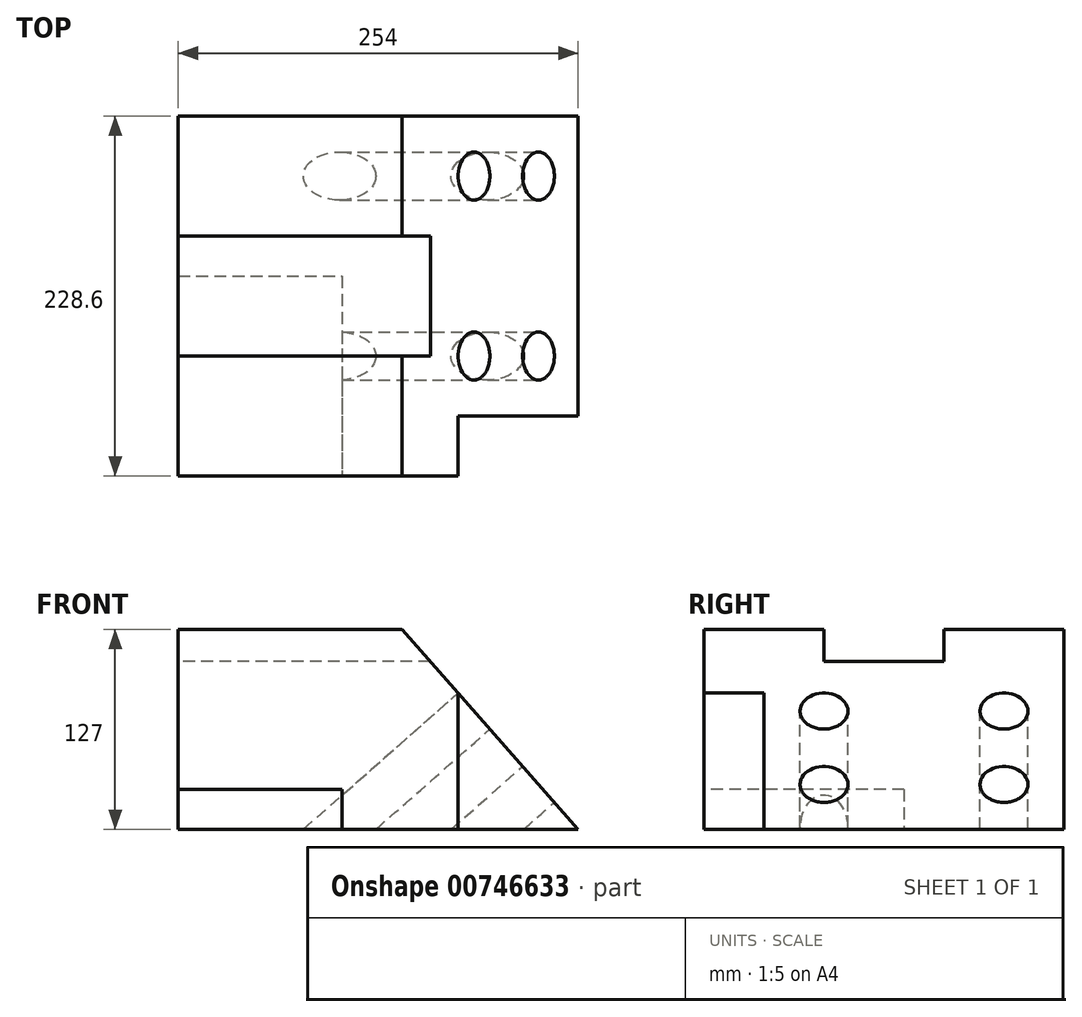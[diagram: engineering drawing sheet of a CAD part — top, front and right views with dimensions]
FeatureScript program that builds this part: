
annotation { "Feature Type Name" : "Feature", "Feature Type Description" : "" }
export const myFeature = defineFeature(function(context is Context, id is Id, definition is map)
    precondition{}
    {
        {
            var Q0;
            Q0=qCreatedBy(makeId("Front.planeOp"),FACE);
            var sketch = newSketch(context, id + "F0", { "sketchPlane" : qUnion([Q0])});
            skLineSegment(sketch, "E0.bottom", {"start": v(-127, 63.5) * mm, "end": v(127, 63.5) * mm});
            skLineSegment(sketch, "E0.top", {"start": v(-127, -63.5) * mm, "end": v(127, -63.5) * mm});
            skLineSegment(sketch, "E0.left", {"start": v(-127, 63.5) * mm, "end": v(-127, -63.5) * mm});
            skLineSegment(sketch, "E0.right", {"start": v(127, 63.5) * mm, "end": v(127, -63.5) * mm});
            skSolve(sketch);
        }
        {
            var Q0;
            Q0=makeQuery(id+"F0.imprint","IMPRINT",FACE,{"disambiguationData":[TD([[makeQuery(id+"F0.imprint","IMPRINT",EDGE,{"derivedFrom":sQuery(id+"F0.wireOp",EDGE,"E0.bottom")}),-1.0]])]});
            extrude(context, id + "F1", {"entities" : qUnion([Q0]), "oppositeDirection" : true, "depth" : 228.6 * mm, "offsetDistance" : 25.4 * mm});
        }
        {
            var Q0;
            Q0=makeQuery(id+"F1.opExtrude","CAP_FACE",FACE,{"disambiguationData":[OSD([sQuery(id+"F0.wireOp",EDGE,"E0.bottom"),sQuery(id+"F0.wireOp",EDGE,"E0.top"),sQuery(id+"F0.wireOp",EDGE,"E0.left"),sQuery(id+"F0.wireOp",EDGE,"E0.right")])],"isStart":true});
            var sketch = newSketch(context, id + "F2", { "sketchPlane" : qUnion([Q0])});
            skLineSegment(sketch, "E1", {"start": v(15.24, 63.5) * mm, "end": v(15.24, -63.5) * mm});
            skLineSegment(sketch, "E2", {"start": v(15.24, -63.5) * mm, "end": v(127, -63.5) * mm});
            skLineSegment(sketch, "E3", {"start": v(127, -63.5) * mm, "end": v(15.24, 63.5) * mm});
            skSolve(sketch);
        }
        {
            var Q0;
            {var subQ0=sQuery(id+"F2.wireOp",EDGE,"E3");Q0=makeQuery(id+"F2.imprint","IMPRINT",FACE,{"disambiguationData":[TD([[makeQuery(id+"F2.imprint","IMPRINT",EDGE,{"derivedFrom":subQ0}),-1.0]])]});}
            extrude(context, id + "F3", {"entities" : qUnion([Q0]), "operationType" : NewBodyOperationType.REMOVE, "oppositeDirection" : true, "depth" : 1270 * mm, "offsetDistance" : 25.4 * mm});
        }
        {
            var Q0;
            Q0=makeQuery(id+"F1.opExtrude","CAP_FACE",FACE,{"disambiguationData":[OSD([sQuery(id+"F0.wireOp",EDGE,"E0.bottom"),sQuery(id+"F0.wireOp",EDGE,"E0.top"),sQuery(id+"F0.wireOp",EDGE,"E0.left"),sQuery(id+"F0.wireOp",EDGE,"E0.right")])],"isStart":true});
            var sketch = newSketch(context, id + "F4", { "sketchPlane" : qUnion([Q0])});
            skLineSegment(sketch, "E4", {"start": v(127, -63.5) * mm, "end": v(50.8, 23.1) * mm});
            skLineSegment(sketch, "E5", {"start": v(50.8, 23.1) * mm, "end": v(50.8, -63.5) * mm});
            skLineSegment(sketch, "E6", {"start": v(50.8, -63.5) * mm, "end": v(127, -63.5) * mm});
            skSolve(sketch);
        }
        {
            var Q0;
            Q0=makeQuery(id+"F4.imprint","IMPRINT",FACE,{"disambiguationData":[TD([[makeQuery(id+"F4.imprint","IMPRINT",EDGE,{"derivedFrom":sQuery(id+"F4.wireOp",EDGE,"E4")}),1.0]])]});
            extrude(context, id + "F5", {"entities" : qUnion([Q0]), "operationType" : NewBodyOperationType.REMOVE, "oppositeDirection" : true, "depth" : 38.1 * mm, "offsetDistance" : 25.4 * mm});
        }
        {
            var Q0;
            Q0=makeQuery(id+"F1.opExtrude","CAP_FACE",FACE,{"disambiguationData":[OSD([sQuery(id+"F0.wireOp",EDGE,"E0.bottom"),sQuery(id+"F0.wireOp",EDGE,"E0.top"),sQuery(id+"F0.wireOp",EDGE,"E0.left"),sQuery(id+"F0.wireOp",EDGE,"E0.right")])],"isStart":true});
            var sketch = newSketch(context, id + "F6", { "sketchPlane" : qUnion([Q0])});
            skLineSegment(sketch, "E7.bottom", {"start": v(-127, -63.5) * mm, "end": v(-22.86, -63.5) * mm});
            skLineSegment(sketch, "E7.top", {"start": v(-127, -38.1) * mm, "end": v(-22.86, -38.1) * mm});
            skLineSegment(sketch, "E7.left", {"start": v(-127, -63.5) * mm, "end": v(-127, -38.1) * mm});
            skLineSegment(sketch, "E7.right", {"start": v(-22.86, -63.5) * mm, "end": v(-22.86, -38.1) * mm});
            skSolve(sketch);
        }
        {
            var Q0;
            Q0=makeQuery(id+"F6.imprint","IMPRINT",FACE,{"disambiguationData":[TD([[makeQuery(id+"F6.imprint","IMPRINT",EDGE,{"derivedFrom":sQuery(id+"F6.wireOp",EDGE,"E7.bottom")}),1.0]])]});
            extrude(context, id + "F7", {"entities" : qUnion([Q0]), "operationType" : NewBodyOperationType.REMOVE, "oppositeDirection" : true, "depth" : 127 * mm, "offsetDistance" : 25.4 * mm});
        }
        {
            var Q0;
            Q0=makeQuery(id+"F3.boolean.opBoolean","COPY",FACE,{"derivedFrom":makeQuery(id+"F3.opExtrude","SWEPT_FACE",FACE,{"disambiguationData":[OSD([sQuery(id+"F2.wireOp",EDGE,"E3")])]})});
            var sketch = newSketch(context, id + "F8", { "sketchPlane" : qUnion([Q0])});
            skCircle(sketch, "E8", {"center": v(76.2, -31.47) * mm, "radius": 15.24 * mm});
            skCircle(sketch, "E9", {"center": v(190.5, -31.47) * mm, "radius": 15.24 * mm});
            skCircle(sketch, "E10", {"center": v(76.2, -93.47) * mm, "radius": 15.24 * mm});
            skCircle(sketch, "E11", {"center": v(190.5, -93.47) * mm, "radius": 15.24 * mm});
            skSolve(sketch);
        }
        {
            var Q0;
            Q0=makeQuery(id+"F8.imprint","IMPRINT",FACE,{"disambiguationData":[TD([[makeQuery(id+"F8.imprint","IMPRINT",EDGE,{"derivedFrom":sQuery(id+"F8.wireOp",EDGE,"E8")}),1.0]])]});
            var Q1;
            Q1=makeQuery(id+"F8.imprint","IMPRINT",FACE,{"disambiguationData":[TD([[makeQuery(id+"F8.imprint","IMPRINT",EDGE,{"derivedFrom":sQuery(id+"F8.wireOp",EDGE,"E9")}),1.0]])]});
            var Q2;
            Q2=makeQuery(id+"F8.imprint","IMPRINT",FACE,{"disambiguationData":[TD([[makeQuery(id+"F8.imprint","IMPRINT",EDGE,{"derivedFrom":sQuery(id+"F8.wireOp",EDGE,"E11")}),1.0]])]});
            var Q3;
            Q3=makeQuery(id+"F8.imprint","IMPRINT",FACE,{"disambiguationData":[TD([[makeQuery(id+"F8.imprint","IMPRINT",EDGE,{"derivedFrom":sQuery(id+"F8.wireOp",EDGE,"E10")}),1.0]])]});
            extrude(context, id + "F9", {"entities" : qUnion([Q0, Q1, Q2, Q3]), "operationType" : NewBodyOperationType.REMOVE, "oppositeDirection" : true, "depth" : 1270 * mm, "offsetDistance" : 25.4 * mm});
        }
        {
            var Q0;
            Q0=makeQuery(id+"F1.opExtrude","SWEPT_FACE",FACE,{"disambiguationData":[OSD([sQuery(id+"F0.wireOp",EDGE,"E0.left")])]});
            var sketch = newSketch(context, id + "F10", { "sketchPlane" : qUnion([Q0])});
            skLineSegment(sketch, "E12.bottom", {"start": v(-152.4, 63.5) * mm, "end": v(-76.2, 63.5) * mm});
            skLineSegment(sketch, "E12.top", {"start": v(-152.4, 43.18) * mm, "end": v(-76.2, 43.18) * mm});
            skLineSegment(sketch, "E12.left", {"start": v(-152.4, 63.5) * mm, "end": v(-152.4, 43.18) * mm});
            skLineSegment(sketch, "E12.right", {"start": v(-76.2, 63.5) * mm, "end": v(-76.2, 43.18) * mm});
            skSolve(sketch);
        }
        {
            var Q0;
            Q0=makeQuery(id+"F10.imprint","IMPRINT",FACE,{"disambiguationData":[TD([[makeQuery(id+"F10.imprint","IMPRINT",EDGE,{"derivedFrom":sQuery(id+"F10.wireOp",EDGE,"E12.bottom")}),-1.0]])]});
            extrude(context, id + "F11", {"entities" : qUnion([Q0]), "operationType" : NewBodyOperationType.REMOVE, "oppositeDirection" : true, "depth" : 1270 * mm, "offsetDistance" : 25.4 * mm});
        }
    });
